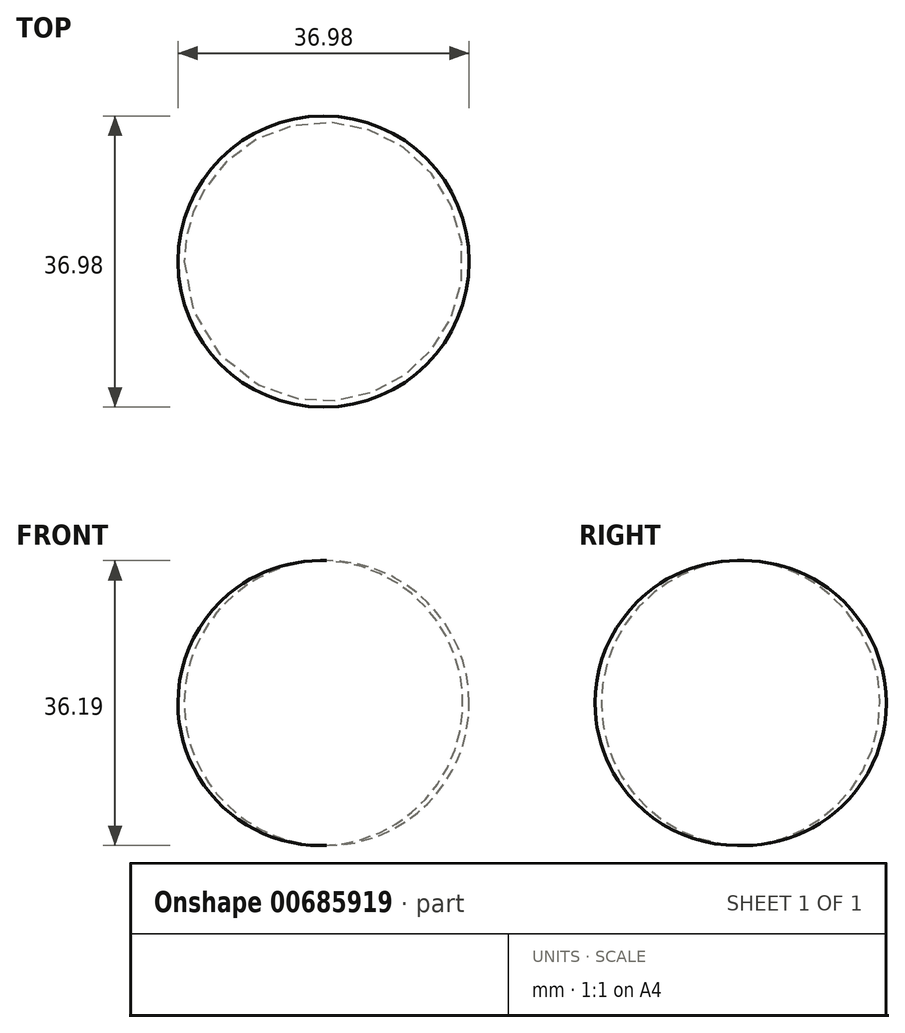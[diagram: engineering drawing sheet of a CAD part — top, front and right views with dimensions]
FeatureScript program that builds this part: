
annotation { "Feature Type Name" : "Feature", "Feature Type Description" : "" }
export const myFeature = defineFeature(function(context is Context, id is Id, definition is map)
    precondition{}
    {
        {
            var Q0;
            Q0=qCreatedBy(makeId("Front.planeOp"),FACE);
            var sketch = newSketch(context, id + "F0", { "sketchPlane" : qUnion([Q0])});
            skArc(sketch, "E0", {"start": v(0, 36.19) * mm, "mid": v(-18.5, 18.1) * mm, "end": v(0, 0) * mm});
            skLineSegment(sketch, "E1", {"start": v(0, 36.19) * mm, "end": v(0, 0) * mm});
            skSolve(sketch);
        }
        {
            var Q0;
            Q0 = qSketchRegion(id + "F0", true);
            var Q1;
            Q1=sQuery(id+"F0.wireOp",EDGE,"E1");
            revolve(context, id + "F1", {"surfaceOperationType" : NewSurfaceOperationType.NEW, "entities" : qUnion([Q0]), "axis" : qUnion([Q1]), "revolveType" : RevolveType.FULL});
        }
    });
